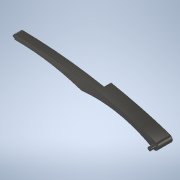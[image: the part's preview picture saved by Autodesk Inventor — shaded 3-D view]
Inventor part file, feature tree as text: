
AUTODESK INVENTOR PART (.ipt)
format: ipt  version: 2021 (Build 250183000, 183)  size: 144,384 bytes
history: native  units: in
note: dims shown in document units (in); Inventor stores cm internally (conversion verified against a paired STEP export)
features: extrude x4, fillet x3, sketch x3, other x1, projected_geometry x1
ambient origin geometry x8: Origin, YZ Plane, XZ Plane, XY Plane, X Axis, Y Axis, Z Axis, Center Point
bodies: Solid1 (feature_tree)
feature tree (12):
  extrude  "Extrusion1"  Depth=0.3937in
  extrude  "Extrusion3"  Depth=0.1575in TaperAngle=0.0deg
  extrude  "Extrusion5"  Depth=0.0591in TaperAngle=0.0deg
  fillet  "Fillet1"  Radius=0.0787in
  fillet  "Arredondamento2"  Radius=0.0787in
  other  "Plano de trabalho2"
  fillet  "Arredondamento3"  Radius=0.0394in
  extrude  "Extrusão8"  Depth=0.0394in
  sketch  "Sketch1"  dims[d0=1.7717in d1=0.3937in]
  sketch  "Sketch3"  dims[d5=0.0787in d6=0.1575in d7=0.0in]
  projected_geometry  "Projected Loop4"
  sketch  "Esboço9"  dims[d10=0.0394in d11=0.0591in d12=0.0in d16=0.0787in d17=0.0in d18=0.0787in d20=0.0394in d21=0.125in d28=0.0394in d29=0.063in d30=0.3937in d31=0.0in]
